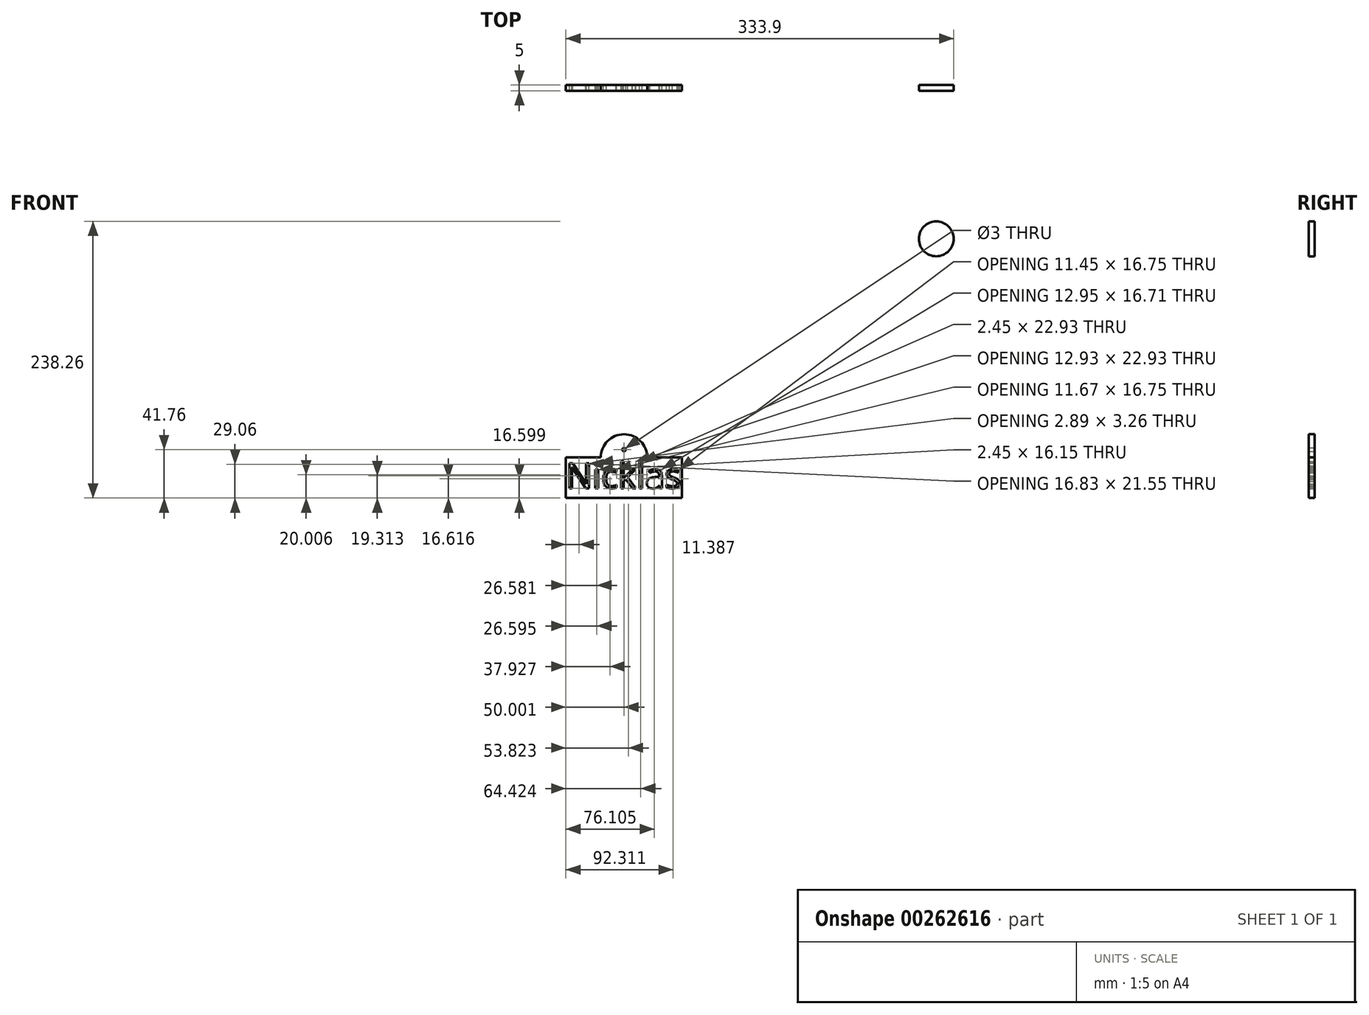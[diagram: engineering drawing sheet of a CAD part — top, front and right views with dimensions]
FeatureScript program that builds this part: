
annotation { "Feature Type Name" : "Feature", "Feature Type Description" : "" }
export const myFeature = defineFeature(function(context is Context, id is Id, definition is map)
    precondition{}
    {
        {
            var Q0;
            Q0=qCreatedBy(makeId("Front.planeOp"),FACE);
            var sketch = newSketch(context, id + "F0", { "sketchPlane" : qUnion([Q0])});
            skLineSegment(sketch, "E0.bottom", {"start": v(-260.9, -170.06) * mm, "end": v(-160.9, -170.06) * mm});
            skLineSegment(sketch, "E0.top", {"start": v(-260.9, -205.06) * mm, "end": v(-160.9, -205.06) * mm});
            skLineSegment(sketch, "E0.left", {"start": v(-260.9, -170.06) * mm, "end": v(-260.9, -205.06) * mm});
            skLineSegment(sketch, "E0.right", {"start": v(-160.9, -170.06) * mm, "end": v(-160.9, -205.06) * mm});
            skArc(sketch, "E1", {"start": v(-190.9, -170.06) * mm, "mid": v(-210.9, -150.06) * mm, "end": v(-230.9, -170.06) * mm});
            skCircle(sketch, "E2", {"center": v(58, 18.2) * mm, "radius": 15 * mm});
            skCircle(sketch, "E3", {"center": v(-210.9, -163.3) * mm, "radius": 1.5 * mm});
            skText(sketch, "E4", { "text": "Nicklas", "fontName": "OpenSans-Regular.ttf"});
            const initialGuessF0  = {"E4": [-0.2609, -0.19652, 1, 0, 0.02173]};
            skSetInitialGuess(sketch, initialGuessF0);
            skSolve(sketch);
        }
        {
            var Q0;
            Q0 = qSketchRegion(id + "F0", true);
            extrude(context, id + "F1", {"entities" : qUnion([Q0]), "depth" : 5 * mm});
        }
    });
